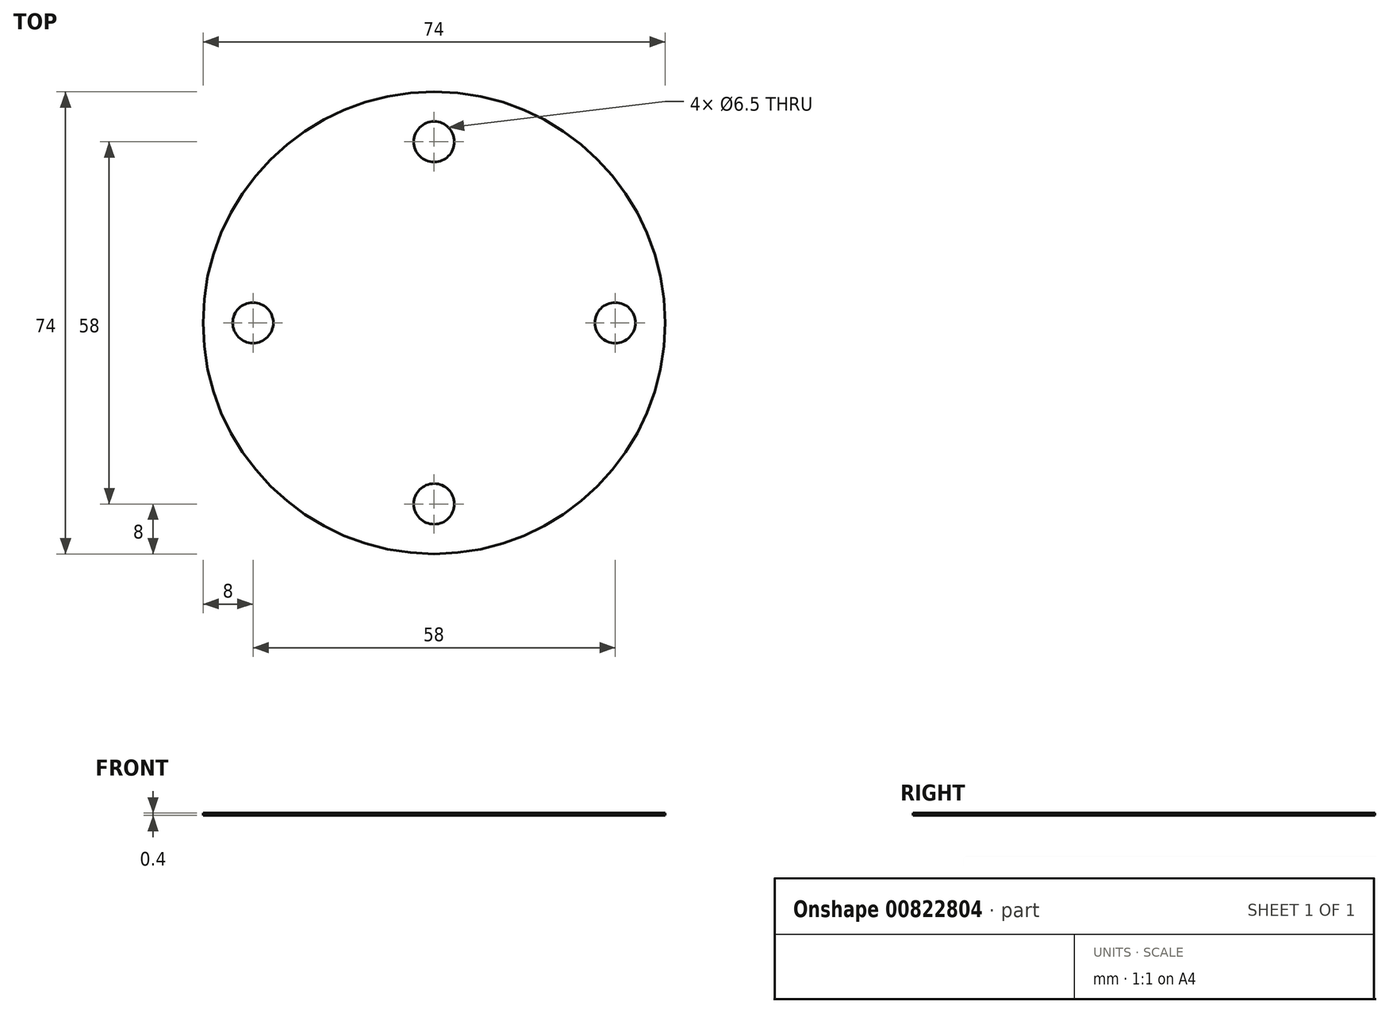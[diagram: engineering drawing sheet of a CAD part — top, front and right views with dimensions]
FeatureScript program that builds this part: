
annotation { "Feature Type Name" : "Feature", "Feature Type Description" : "" }
export const myFeature = defineFeature(function(context is Context, id is Id, definition is map)
    precondition{}
    {
        {
            var Q0;
            Q0=qCreatedBy(makeId("Top.planeOp"),FACE);
            var sketch = newSketch(context, id + "F0", { "sketchPlane" : qUnion([Q0])});
            skCircle(sketch, "E0", {"center": v(0, 0) * mm, "radius": 16 * mm, "construction": true});
            skCircle(sketch, "E1", {"center": v(0, 0) * mm, "radius": 29 * mm, "construction": true});
            skCircle(sketch, "E2", {"center": v(0, 0) * mm, "radius": 37 * mm});
            skLineSegment(sketch, "E3", {"start": v(0, -37) * mm, "end": v(0, 37) * mm, "construction": true});
            skLineSegment(sketch, "E4", {"start": v(0, 37) * mm, "end": v(37, 0) * mm, "construction": true});
            skLineSegment(sketch, "E5", {"start": v(37, 0) * mm, "end": v(-37, 0) * mm, "construction": true});
            skCircle(sketch, "E6", {"center": v(0, 29) * mm, "radius": 3.25 * mm});
            skCircle(sketch, "E7", {"center": v(-29, 0) * mm, "radius": 3.25 * mm});
            skCircle(sketch, "E8", {"center": v(0, -29) * mm, "radius": 3.25 * mm});
            skCircle(sketch, "E9", {"center": v(29, 0) * mm, "radius": 3.25 * mm});
            skSolve(sketch);
        }
        {
            var Q0;
            Q0=qSketchRegion(id+"F0",true);
            extrude(context, id + "F1", {"entities" : qUnion([Q0]), "depth" : 0.4 * mm, "offsetDistance" : 25 * mm});
        }
    });
